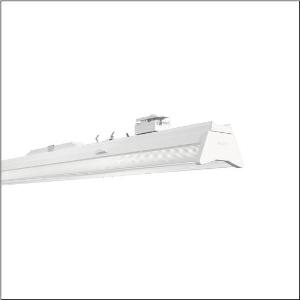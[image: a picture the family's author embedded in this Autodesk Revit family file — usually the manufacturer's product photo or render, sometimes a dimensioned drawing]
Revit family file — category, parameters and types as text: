
# Revit family: licross_r__21_performance_mo_52td16cn445g_c2c6
name_source: partatom
category: Lighting Fixtures
units: mm (PartAtom-declared; Revit-internal decimal feet)

## family parameters
Cut with Voids When Loaded = No
Host = Face
Light Source = No
Part Type = Normal
Room Calculation Point = No
Round Connector Dimension = Use Diameter
Shared = No

## types (1)
- --- (1 x LED, 4500 lm, 24.1 W, 4000K)
    Apparent Load = 24 VA
    CIE Flux Codes = 66 88 96 79 100
    Color Rendering = 80
    Color Temperature = 4000K
    Default Elevation = 1800 mm
    Description = Licross® 21 Performance MO, luminaire insert, of sheet steel, galvanised, coil coated, white, length: 1.500mm, width: 120mm, height: 123mm, LED rated luminous flux: 4.500lm, light colour: 840, SDCM (Standard Deviation of Colour Matching)MacAdam ≤ 3 SDCM (initial), control gear: ON/OFF Multilumen, CLOi, with plug, 3-pole, with phase selection, mains connection: 220..240V, AC, 50/60Hz, start of lifetime: 24W, end of service life: 28W, internal wiring halogen-free, primary light control with lens, of plastic, primary optical cover: cover, of PMMA, CAT 2 (L<= 3000cd/m²), light emission: direct/indirect distribution, primary light characteristic: symmetric, protection rating (complete): IP54, insulation class (complete): insulation class I (protective earthing), certification: CE, ENEC, UKCA, protection symbol: D if used in an environment with non-conductive dust loads with corresponding accessories, impact resistance: IK06, permissible ambient temperature for indoor applications: -35..+55°C, corresponds to IFS (International Featured Standards) requirements for safety and quality in the food industry, reducing of maximum allowable ambient temperature of 5°C with ceiling mounting, LABS conformity tested according to VDMA 24364:2018-05, packaging unit: 1 piece
    Height = 114 mm
    Lamp = 1 x LED
    Lamp Light Flux = 4500 lm
    Lamp Power = 24.1 W
    Lamp count = 1
    Length = 1500 mm
    Luminous efficacy = 187 lm/W
    Manufacturer = Siteco
    ModVariant = No
    Model = 52TD16CN445G
    Mounting Place = Ceiling
    Mounting Type = Pendant
    Number of Poles = 1
    OnlyDefault = Yes
    Power Factor = 1
    Product Name = Licross® 21 Performance MO
    Product group = luminaire insert | ceiling pendant
    ProductGroupID = 901
    Protection Class = Protection class I
    Protection Degree = IP 54
    RLX_Detail_Level = 1
    RLX_Emergency_Light_Flux = 0 lm
    RLX_Emergency_Type = 0
    RLX_Emergency_Type_DB = No
    RlxData = <blob elided: 31525 chars, md5=2b5c68c0>
    Socket = socket
    Standby Power = 0 W
    System Light Flux = 4500 lm
    System Power = 24 W
    Type Comments = factory setting: luminous flux: 100 % | (A | C | E) | 55 mA
    Type Image = l_1256138.jpg
    URL = http://relux.com
    VarID = @adj_058819
    Voltage = 0 V
    Weight = 0.00 kg
    Width = 120 mm

## geometry (parser evidence)
native form markers: Blend x4, Sweep x10
no freeform markers — native parametric forms only
